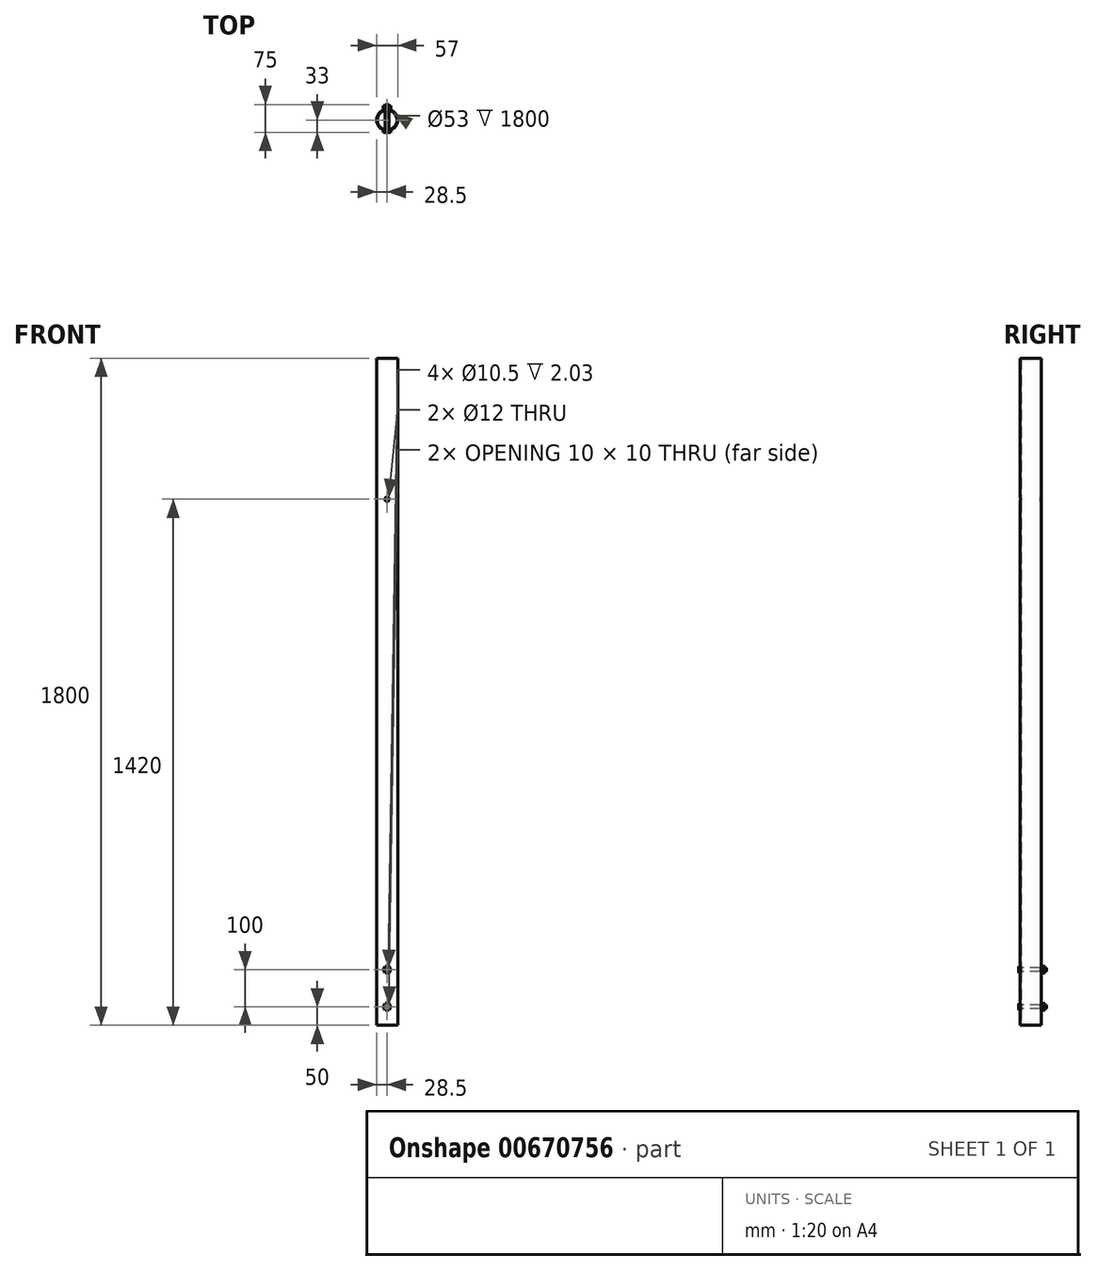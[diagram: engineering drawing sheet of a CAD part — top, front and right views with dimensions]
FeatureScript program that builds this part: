
annotation { "Feature Type Name" : "Feature", "Feature Type Description" : "" }
export const myFeature = defineFeature(function(context is Context, id is Id, definition is map)
    precondition{}
    {
        {
            var Q0;
            Q0=qCreatedBy(makeId("Top.planeOp"),FACE);
            var sketch = newSketch(context, id + "F0", { "sketchPlane" : qUnion([Q0])});
            skCircle(sketch, "E0", {"center": v(0, 0) * mm, "radius": 28.5 * mm});
            skCircle(sketch, "E1", {"center": v(0, 0) * mm, "radius": 26.5 * mm});
            skSolve(sketch);
        }
        {
            var Q0;
            Q0 = qSketchRegion(id + "F0", true);
            extrude(context, id + "F1", {"entities" : qUnion([Q0]), "depth" : 1800 * mm, "offsetDistance" : 25 * mm});
        }
        {
            var Q0;
            Q0=qCreatedBy(makeId("Front.planeOp"),FACE);
            var sketch = newSketch(context, id + "F2", { "sketchPlane" : qUnion([Q0])});
            skCircle(sketch, "E2", {"center": v(0, 50) * mm, "radius": 5.25 * mm});
            skCircle(sketch, "E3", {"center": v(0, 150) * mm, "radius": 5.25 * mm});
            skCircle(sketch, "E4", {"center": v(0, 1420) * mm, "radius": 6 * mm});
            skSolve(sketch);
        }
        {
            var Q0;
            Q0 = qSketchRegion(id + "F2", true);
            extrude(context, id + "F3", {"entities" : qUnion([Q0]), "operationType" : NewBodyOperationType.REMOVE, "endBound" : BoundingType.THROUGH_ALL, "oppositeDirection" : true, "depth" : 25 * mm, "offsetDistance" : 25 * mm, "hasSecondDirection" : true, "secondDirectionBound" : SecondDirectionBoundingType.THROUGH_ALL, "secondDirectionOppositeDirection" : false, "secondDirectionDepth" : 25 * mm});
        }
        {
            var Q0;
            Q0=qCreatedBy(makeId("Front.planeOp"),FACE);
            cPlane(context, id + "F4", {"entities" : qUnion([Q0]), "cplaneType" : CPlaneType.OFFSET, "offset" : 28 * mm, "width" : 150 * mm, "height" : 150 * mm});
        }
        {
            var Q0;
            Q0=qCreatedBy(id+"F4.planeOp",FACE);
            var sketch = newSketch(context, id + "F5", { "sketchPlane" : qUnion([Q0])});
            skCircle(sketch, "E5.cCircle", {"center": v(0, 50) * mm, "radius": 10 * mm, "construction": true});
            skLineSegment(sketch, "E5.0", {"start": v(5, 41.34) * mm, "end": v(-5, 41.34) * mm});
            skLineSegment(sketch, "E5.1", {"start": v(-5, 41.34) * mm, "end": v(-10, 50) * mm});
            skLineSegment(sketch, "E5.2", {"start": v(-10, 50) * mm, "end": v(-5, 58.66) * mm});
            skLineSegment(sketch, "E5.3", {"start": v(-5, 58.66) * mm, "end": v(5, 58.66) * mm});
            skLineSegment(sketch, "E5.4", {"start": v(5, 58.66) * mm, "end": v(10, 50) * mm});
            skLineSegment(sketch, "E5.5", {"start": v(10, 50) * mm, "end": v(5, 41.34) * mm});
            skCircle(sketch, "E6.cCircle", {"center": v(0, 150) * mm, "radius": 10 * mm, "construction": true});
            skLineSegment(sketch, "E6.0", {"start": v(5, 141.34) * mm, "end": v(-5, 141.34) * mm});
            skLineSegment(sketch, "E6.1", {"start": v(-5, 141.34) * mm, "end": v(-10, 150) * mm});
            skLineSegment(sketch, "E6.2", {"start": v(-10, 150) * mm, "end": v(-5, 158.66) * mm});
            skLineSegment(sketch, "E6.3", {"start": v(-5, 158.66) * mm, "end": v(5, 158.66) * mm});
            skLineSegment(sketch, "E6.4", {"start": v(5, 158.66) * mm, "end": v(10, 150) * mm});
            skLineSegment(sketch, "E6.5", {"start": v(10, 150) * mm, "end": v(5, 141.34) * mm});
            skSolve(sketch);
        }
        {
            var Q0;
            Q0 = qSketchRegion(id + "F5", true);
            extrude(context, id + "F6", {"entities" : qUnion([Q0]), "operationType" : NewBodyOperationType.ADD, "depth" : 5 * mm, "offsetDistance" : 25 * mm});
        }
        {
            var Q0;
            Q0=qCreatedBy(id+"F4.planeOp",FACE);
            var sketch = newSketch(context, id + "F7", { "sketchPlane" : qUnion([Q0])});
            skCircle(sketch, "E7", {"center": v(0, 150) * mm, "radius": 5 * mm});
            skCircle(sketch, "E8", {"center": v(0, 50) * mm, "radius": 5 * mm});
            skSolve(sketch);
        }
        {
            var Q0;
            Q0 = qSketchRegion(id + "F7", true);
            extrude(context, id + "F8", {"entities" : qUnion([Q0]), "operationType" : NewBodyOperationType.ADD, "oppositeDirection" : true, "depth" : 70 * mm, "offsetDistance" : 25 * mm});
        }
        {
            var Q0;
            Q0=qCreatedBy(makeId("Front.planeOp"),FACE);
            cPlane(context, id + "F9", {"entities" : qUnion([Q0]), "cplaneType" : CPlaneType.OFFSET, "offset" : 28 * mm, "oppositeDirection" : true, "width" : 150 * mm, "height" : 150 * mm});
        }
        {
            var Q0;
            Q0=qCreatedBy(id+"F9.planeOp",FACE);
            var sketch = newSketch(context, id + "F10", { "sketchPlane" : qUnion([Q0])});
            skLineSegment(sketch, "E9.0.0", {"start": v(5, 141.34) * mm, "end": v(10, 150) * mm});
            skLineSegment(sketch, "E9.0.1", {"start": v(10, 150) * mm, "end": v(5, 158.66) * mm});
            skLineSegment(sketch, "E9.0.2", {"start": v(5, 158.66) * mm, "end": v(-5, 158.66) * mm});
            skLineSegment(sketch, "E9.0.3", {"start": v(-5, 158.66) * mm, "end": v(-10, 150) * mm});
            skLineSegment(sketch, "E9.0.4", {"start": v(-10, 150) * mm, "end": v(-5, 141.34) * mm});
            skLineSegment(sketch, "E9.0.5", {"start": v(-5, 141.34) * mm, "end": v(5, 141.34) * mm});
            skLineSegment(sketch, "E10.0.0", {"start": v(5, 41.34) * mm, "end": v(10, 50) * mm});
            skLineSegment(sketch, "E10.0.1", {"start": v(10, 50) * mm, "end": v(5, 58.66) * mm});
            skLineSegment(sketch, "E10.0.2", {"start": v(5, 58.66) * mm, "end": v(-5, 58.66) * mm});
            skLineSegment(sketch, "E10.0.3", {"start": v(-5, 58.66) * mm, "end": v(-10, 50) * mm});
            skLineSegment(sketch, "E10.0.4", {"start": v(-10, 50) * mm, "end": v(-5, 41.34) * mm});
            skLineSegment(sketch, "E10.0.5", {"start": v(-5, 41.34) * mm, "end": v(5, 41.34) * mm});
            skSolve(sketch);
        }
        {
            var Q0;
            Q0 = qSketchRegion(id + "F10", true);
            extrude(context, id + "F11", {"entities" : qUnion([Q0]), "operationType" : NewBodyOperationType.ADD, "oppositeDirection" : true, "depth" : 5 * mm, "offsetDistance" : 25 * mm});
        }
        {
            var Q0;
            Q0=makeQuery(id+"F11.opExtrude","CAP_FACE",FACE,{"disambiguationData":[OSD([sQuery(id+"F10.wireOp",EDGE,"E9.0.0"),sQuery(id+"F10.wireOp",EDGE,"E9.0.1"),sQuery(id+"F10.wireOp",EDGE,"E9.0.2"),sQuery(id+"F10.wireOp",EDGE,"E9.0.3"),sQuery(id+"F10.wireOp",EDGE,"E9.0.4"),sQuery(id+"F10.wireOp",EDGE,"E9.0.5")])],"isStart":false});
            cPlane(context, id + "F12", {"entities" : qUnion([Q0]), "cplaneType" : CPlaneType.OFFSET, "offset" : 1 * mm, "width" : 150 * mm, "height" : 150 * mm});
        }
        {
            var Q0;
            Q0=qCreatedBy(id+"F12.planeOp",FACE);
            var sketch = newSketch(context, id + "F13", { "sketchPlane" : qUnion([Q0])});
            skLineSegment(sketch, "E11.0.0", {"start": v(-5, 141.34) * mm, "end": v(-10, 150) * mm});
            skLineSegment(sketch, "E11.0.1", {"start": v(-10, 150) * mm, "end": v(-5, 158.66) * mm});
            skLineSegment(sketch, "E11.0.2", {"start": v(-5, 158.66) * mm, "end": v(5, 158.66) * mm});
            skLineSegment(sketch, "E11.0.3", {"start": v(5, 158.66) * mm, "end": v(10, 150) * mm});
            skLineSegment(sketch, "E11.0.4", {"start": v(10, 150) * mm, "end": v(5, 141.34) * mm});
            skLineSegment(sketch, "E11.0.5", {"start": v(5, 141.34) * mm, "end": v(-5, 141.34) * mm});
            skLineSegment(sketch, "E12.0.0", {"start": v(-5, 41.34) * mm, "end": v(-10, 50) * mm});
            skLineSegment(sketch, "E12.0.1", {"start": v(-10, 50) * mm, "end": v(-5, 58.66) * mm});
            skLineSegment(sketch, "E12.0.2", {"start": v(-5, 58.66) * mm, "end": v(5, 58.66) * mm});
            skLineSegment(sketch, "E12.0.3", {"start": v(5, 58.66) * mm, "end": v(10, 50) * mm});
            skLineSegment(sketch, "E12.0.4", {"start": v(10, 50) * mm, "end": v(5, 41.34) * mm});
            skLineSegment(sketch, "E12.0.5", {"start": v(5, 41.34) * mm, "end": v(-5, 41.34) * mm});
            skSolve(sketch);
        }
        {
            var Q0;
            Q0 = qSketchRegion(id + "F13", true);
            extrude(context, id + "F14", {"entities" : qUnion([Q0]), "operationType" : NewBodyOperationType.ADD, "depth" : 5 * mm, "offsetDistance" : 25 * mm});
        }
    });
